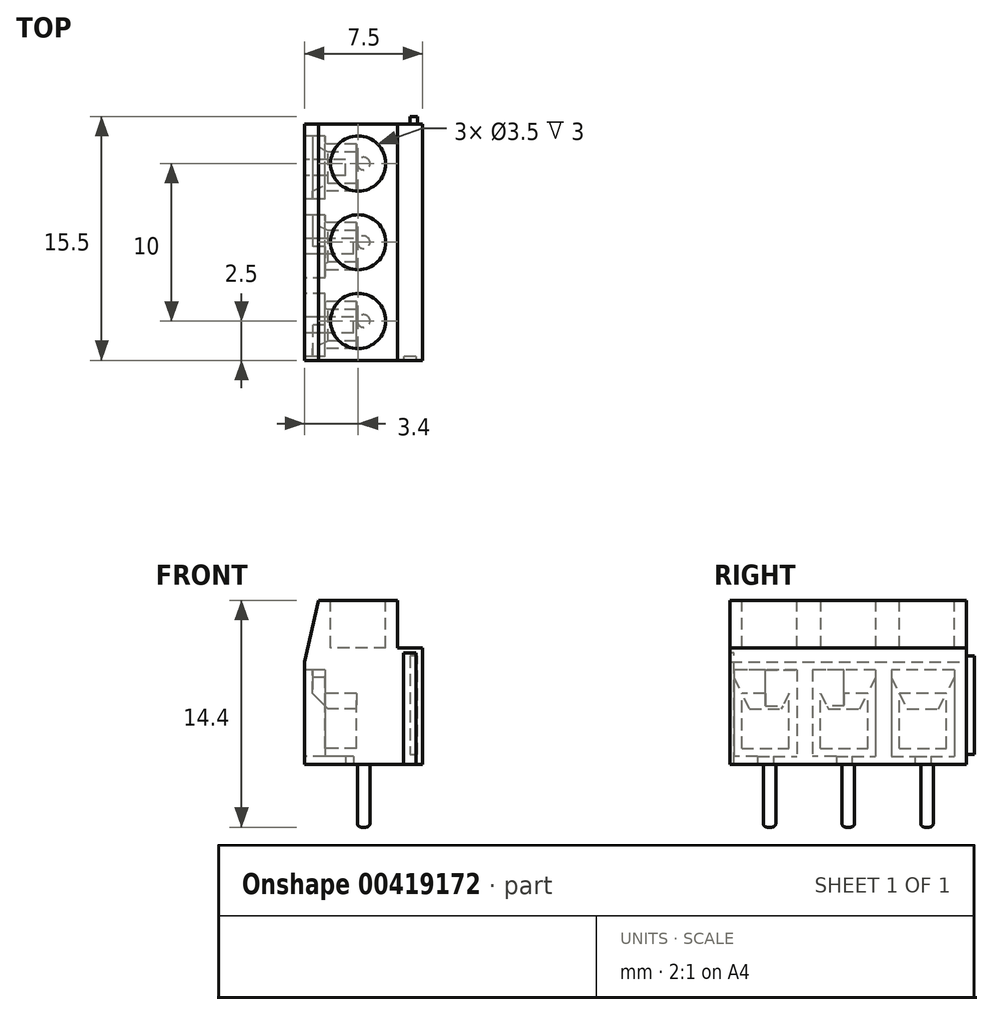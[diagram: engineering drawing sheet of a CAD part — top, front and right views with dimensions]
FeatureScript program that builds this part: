
annotation { "Feature Type Name" : "Feature", "Feature Type Description" : "" }
export const myFeature = defineFeature(function(context is Context, id is Id, definition is map)
    precondition{}
    {
        {
            var Q0;
            Q0=qCreatedBy(makeId("Front.planeOp"),FACE);
            var sketch = newSketch(context, id + "F0", { "sketchPlane" : qUnion([Q0])});
            skLineSegment(sketch, "E0", {"start": v(0, 0) * mm, "end": v(-7.5, 0) * mm});
            skLineSegment(sketch, "E1", {"start": v(-7.5, 0) * mm, "end": v(-7.5, 6.5) * mm});
            skLineSegment(sketch, "E2", {"start": v(-7.5, 6.5) * mm, "end": v(-6.6, 10.4) * mm});
            skLineSegment(sketch, "E3", {"start": v(-6.6, 10.4) * mm, "end": v(-1.6, 10.4) * mm});
            skLineSegment(sketch, "E4", {"start": v(-1.6, 10.4) * mm, "end": v(-1.6, 7.4) * mm});
            skLineSegment(sketch, "E5", {"start": v(-1.6, 7.4) * mm, "end": v(0, 7.4) * mm});
            skLineSegment(sketch, "E6", {"start": v(0, 7.4) * mm, "end": v(0, 0) * mm});
            skSolve(sketch);
        }
        {
            var Q0;
            Q0 = qSketchRegion(id + "F0", true);
            extrude(context, id + "F1", {"entities" : qUnion([Q0]), "depth" : 15 * mm});
        }
        {
            var Q0;
            Q0=makeQuery(id+"F1.opExtrude","SWEPT_FACE",FACE,{"disambiguationData":[OSD([sQuery(id+"F0.wireOp",EDGE,"E3")])]});
            var sketch = newSketch(context, id + "F2", { "sketchPlane" : qUnion([Q0])});
            skLineSegment(sketch, "E7", {"start": v(-4.1, 0) * mm, "end": v(-4.1, -15) * mm});
            skLineSegment(sketch, "E8", {"start": v(-4.1, -15) * mm, "end": v(-4.1, -7.5) * mm});
            skCircle(sketch, "E9", {"center": v(-4.1, -7.5) * mm, "radius": 1.75 * mm});
            skLineSegment(sketch, "E10", {"start": v(-4.1, -7.5) * mm, "end": v(-4.1, -2.5) * mm});
            skCircle(sketch, "E11", {"center": v(-4.1, -2.5) * mm, "radius": 1.75 * mm});
            skLineSegment(sketch, "E12", {"start": v(-4.1, -7.5) * mm, "end": v(4.92, -7.5) * mm});
            skCircle(sketch, "E13.MirrorC", {"center": v(-4.1, -12.5) * mm, "radius": 1.75 * mm});
            skSolve(sketch);
        }
        {
            var Q0;
            Q0 = qSketchRegion(id + "F2", true);
            extrude(context, id + "F3", {"entities" : qUnion([Q0]), "operationType" : NewBodyOperationType.REMOVE, "oppositeDirection" : true, "depth" : 3 * mm});
        }
        {
            var Q0;
            Q0=makeQuery(id+"F1.opExtrude","SWEPT_FACE",FACE,{"disambiguationData":[OSD([sQuery(id+"F0.wireOp",EDGE,"E1")])]});
            var sketch = newSketch(context, id + "F4", { "sketchPlane" : qUnion([Q0])});
            skLineSegment(sketch, "E14", {"start": v(0, 0) * mm, "end": v(15, 0) * mm});
            skLineSegment(sketch, "E15", {"start": v(15, 0) * mm, "end": v(7.76, 0) * mm});
            skLineSegment(sketch, "E16", {"start": v(7.76, 0) * mm, "end": v(7.76, 0.5) * mm});
            skLineSegment(sketch, "E17", {"start": v(7.76, 0.5) * mm, "end": v(7.76, 1) * mm});
            skLineSegment(sketch, "E18", {"start": v(7.76, 1) * mm, "end": v(7.76, 3.5) * mm});
            skLineSegment(sketch, "E19", {"start": v(7.76, 3.5) * mm, "end": v(7.76, 5.5) * mm});
            skLineSegment(sketch, "E20", {"start": v(7.76, 5.5) * mm, "end": v(7.76, 6) * mm});
            skLineSegment(sketch, "E21", {"start": v(7.76, 6) * mm, "end": v(9.76, 6) * mm});
            skLineSegment(sketch, "E22", {"start": v(9.76, 6) * mm, "end": v(9.76, 0.5) * mm});
            skLineSegment(sketch, "E23", {"start": v(7.76, 0.5) * mm, "end": v(9.76, 0.5) * mm});
            skLineSegment(sketch, "E24", {"start": v(9.76, 6) * mm, "end": v(9.76, 5.5) * mm});
            skLineSegment(sketch, "E25", {"start": v(9.76, 5.5) * mm, "end": v(8.76, 3.5) * mm});
            skLineSegment(sketch, "E26", {"start": v(7.76, 3.5) * mm, "end": v(8.76, 3.5) * mm});
            skLineSegment(sketch, "E27", {"start": v(7.76, 1) * mm, "end": v(9.26, 1) * mm});
            skLineSegment(sketch, "E28", {"start": v(9.26, 1) * mm, "end": v(9.26, 4.5) * mm});
            skLineSegment(sketch, "E29", {"start": v(8.26, 0.5) * mm, "end": v(8.26, 0) * mm});
            skLineSegment(sketch, "E30.MirrorCS", {"start": v(5.76, 6) * mm, "end": v(5.76, 5.5) * mm});
            skLineSegment(sketch, "E31.MirrorCS", {"start": v(7.26, 0.5) * mm, "end": v(7.26, 0) * mm});
            skLineSegment(sketch, "E32.MirrorCS", {"start": v(7.76, 1) * mm, "end": v(6.26, 1) * mm});
            skLineSegment(sketch, "E33.MirrorCS", {"start": v(5.76, 6) * mm, "end": v(5.76, 0.5) * mm});
            skLineSegment(sketch, "E34.MirrorCS", {"start": v(7.76, 0.5) * mm, "end": v(5.76, 0.5) * mm});
            skLineSegment(sketch, "E35.MirrorCS", {"start": v(7.76, 6) * mm, "end": v(5.76, 6) * mm});
            skLineSegment(sketch, "E36.MirrorCS", {"start": v(7.76, 3.5) * mm, "end": v(6.76, 3.5) * mm});
            skLineSegment(sketch, "E37.MirrorCS", {"start": v(6.26, 1) * mm, "end": v(6.26, 4.5) * mm});
            skLineSegment(sketch, "E38.MirrorCS", {"start": v(5.76, 5.5) * mm, "end": v(6.76, 3.5) * mm});
            skLineSegment(sketch, "E39.1.0.0", {"start": v(12.76, 1) * mm, "end": v(14.26, 1) * mm});
            skLineSegment(sketch, "E39.1.0.1", {"start": v(14.26, 1) * mm, "end": v(14.26, 4.5) * mm});
            skLineSegment(sketch, "E39.1.0.2", {"start": v(14.76, 5.5) * mm, "end": v(13.76, 3.5) * mm});
            skLineSegment(sketch, "E39.1.0.3", {"start": v(14.76, 6) * mm, "end": v(14.76, 5.5) * mm});
            skLineSegment(sketch, "E39.1.0.4", {"start": v(12.76, 0.5) * mm, "end": v(14.76, 0.5) * mm});
            skLineSegment(sketch, "E39.1.0.5", {"start": v(12.76, 6) * mm, "end": v(14.76, 6) * mm});
            skLineSegment(sketch, "E39.1.0.6", {"start": v(14.76, 6) * mm, "end": v(14.76, 0.5) * mm});
            skLineSegment(sketch, "E39.1.0.7", {"start": v(12.76, 5.5) * mm, "end": v(12.76, 6) * mm});
            skLineSegment(sketch, "E39.1.0.8", {"start": v(10.76, 6) * mm, "end": v(10.76, 0.5) * mm});
            skLineSegment(sketch, "E39.1.0.9", {"start": v(12.76, 1) * mm, "end": v(11.26, 1) * mm});
            skLineSegment(sketch, "E39.1.0.10", {"start": v(10.76, 6) * mm, "end": v(10.76, 5.5) * mm});
            skLineSegment(sketch, "E39.1.0.11", {"start": v(12.76, 3.5) * mm, "end": v(11.76, 3.5) * mm});
            skLineSegment(sketch, "E39.1.0.12", {"start": v(12.76, 6) * mm, "end": v(10.76, 6) * mm});
            skLineSegment(sketch, "E39.1.0.13", {"start": v(12.76, 3.5) * mm, "end": v(13.76, 3.5) * mm});
            skLineSegment(sketch, "E39.1.0.14", {"start": v(10.76, 5.5) * mm, "end": v(11.76, 3.5) * mm});
            skLineSegment(sketch, "E39.1.0.15", {"start": v(12.76, 0.5) * mm, "end": v(10.76, 0.5) * mm});
            skLineSegment(sketch, "E39.1.0.16", {"start": v(12.76, 1) * mm, "end": v(12.76, 3.5) * mm});
            skLineSegment(sketch, "E39.1.0.17", {"start": v(12.76, 3.5) * mm, "end": v(12.76, 5.5) * mm});
            skLineSegment(sketch, "E39.1.0.18", {"start": v(11.26, 1) * mm, "end": v(11.26, 4.5) * mm});
            skLineSegment(sketch, "E39.1.0.19", {"start": v(12.26, 0.5) * mm, "end": v(12.26, 0) * mm});
            skLineSegment(sketch, "E39.1.0.20", {"start": v(13.26, 0.5) * mm, "end": v(13.26, 0) * mm});
            skLineSegment(sketch, "E39.1.0.21", {"start": v(12.76, 1) * mm, "end": v(12.76, 3.5) * mm});
            skLineSegment(sketch, "E39.1.0.22", {"start": v(12.76, 5.5) * mm, "end": v(12.76, 6) * mm});
            skLineSegment(sketch, "E39.1.0.23", {"start": v(12.76, 0) * mm, "end": v(12.76, 0.5) * mm});
            skLineSegment(sketch, "E39.1.0.24", {"start": v(12.76, 0) * mm, "end": v(12.76, 0.5) * mm});
            skLineSegment(sketch, "E39.1.0.25", {"start": v(12.76, 0.5) * mm, "end": v(12.76, 1) * mm});
            skLineSegment(sketch, "E39.1.0.26", {"start": v(12.76, 0.5) * mm, "end": v(12.76, 1) * mm});
            skLineSegment(sketch, "E39.direction1", {"start": v(5.76, 0.5) * mm, "end": v(10.76, 0.5) * mm, "construction": true});
            skLineSegment(sketch, "E40.MirrorCS", {"start": v(2.76, 0.5) * mm, "end": v(2.76, 1) * mm});
            skLineSegment(sketch, "E41.MirrorCS", {"start": v(2.76, 5.5) * mm, "end": v(2.76, 6) * mm});
            skLineSegment(sketch, "E42.MirrorCS", {"start": v(2.76, 0) * mm, "end": v(2.76, 0.5) * mm});
            skLineSegment(sketch, "E43.MirrorCS", {"start": v(4.76, 6) * mm, "end": v(4.76, 5.5) * mm});
            skLineSegment(sketch, "E44.MirrorCS", {"start": v(0.76, 6) * mm, "end": v(0.76, 5.5) * mm});
            skLineSegment(sketch, "E45.MirrorCS", {"start": v(2.76, 3.5) * mm, "end": v(1.76, 3.5) * mm});
            skLineSegment(sketch, "E46.MirrorCS", {"start": v(2.26, 0.5) * mm, "end": v(2.26, 0) * mm});
            skLineSegment(sketch, "E47.MirrorCS", {"start": v(3.26, 0.5) * mm, "end": v(3.26, 0) * mm});
            skLineSegment(sketch, "E48.MirrorCS", {"start": v(2.76, 1) * mm, "end": v(2.76, 3.5) * mm});
            skLineSegment(sketch, "E49.MirrorCS", {"start": v(2.76, 0.5) * mm, "end": v(0.76, 0.5) * mm});
            skLineSegment(sketch, "E50.MirrorCS", {"start": v(2.76, 3.5) * mm, "end": v(2.76, 5.5) * mm});
            skLineSegment(sketch, "E51.MirrorCS", {"start": v(1.26, 1) * mm, "end": v(1.26, 4.5) * mm});
            skLineSegment(sketch, "E52.MirrorCS", {"start": v(4.76, 6) * mm, "end": v(4.76, 0.5) * mm});
            skLineSegment(sketch, "E53.MirrorCS", {"start": v(2.76, 3.5) * mm, "end": v(3.76, 3.5) * mm});
            skLineSegment(sketch, "E54.MirrorCS", {"start": v(2.76, 0.5) * mm, "end": v(4.76, 0.5) * mm});
            skLineSegment(sketch, "E55.MirrorCS", {"start": v(4.76, 5.5) * mm, "end": v(3.76, 3.5) * mm});
            skLineSegment(sketch, "E56.MirrorCS", {"start": v(0.76, 6) * mm, "end": v(0.76, 0.5) * mm});
            skLineSegment(sketch, "E57.MirrorCS", {"start": v(2.76, 6) * mm, "end": v(4.76, 6) * mm});
            skLineSegment(sketch, "E58.MirrorCS", {"start": v(2.76, 1) * mm, "end": v(4.26, 1) * mm});
            skLineSegment(sketch, "E59.MirrorCS", {"start": v(0.76, 5.5) * mm, "end": v(1.76, 3.5) * mm});
            skLineSegment(sketch, "E60.MirrorCS", {"start": v(4.26, 1) * mm, "end": v(4.26, 4.5) * mm});
            skLineSegment(sketch, "E61.MirrorCS", {"start": v(2.76, 1) * mm, "end": v(1.26, 1) * mm});
            skLineSegment(sketch, "E62.MirrorCS", {"start": v(2.76, 6) * mm, "end": v(0.76, 6) * mm});
            skSolve(sketch);
        }
        {
            var Q0;
            Q0 = qSketchRegion(id + "F4", true);
            var Q1;
            {var subQ2=sQuery(id+"F4.wireOp",EDGE,"E45.MirrorCS");Q1=makeQuery(id+"F4.imprint","IMPRINT",FACE,{"disambiguationData":[TD([[makeQuery(id+"F4.imprint","IMPRINT",EDGE,{"derivedFrom":subQ2}),1.0]])]});}
            var Q2;
            {var subQ1=sQuery(id+"F4.wireOp",EDGE,"E53.MirrorCS");Q2=makeQuery(id+"F4.imprint","IMPRINT",FACE,{"disambiguationData":[TD([[makeQuery(id+"F4.imprint","IMPRINT",EDGE,{"derivedFrom":subQ1}),-1.0]])]});}
            var Q3;
            Q3=makeQuery(id+"F4.imprint","IMPRINT",FACE,{"disambiguationData":[TD([[makeQuery(id+"F4.imprint","IMPRINT",EDGE,{"derivedFrom":sQuery(id+"F4.wireOp",EDGE,"E32.MirrorCS")}),-1.0]])]});
            var Q4;
            {var subQ1=sQuery(id+"F4.wireOp",EDGE,"E26");Q4=makeQuery(id+"F4.imprint","IMPRINT",FACE,{"disambiguationData":[TD([[makeQuery(id+"F4.imprint","IMPRINT",EDGE,{"derivedFrom":subQ1}),-1.0]])]});}
            var Q5;
            Q5=makeQuery(id+"F4.imprint","IMPRINT",FACE,{"disambiguationData":[TD([[makeQuery(id+"F4.imprint","IMPRINT",EDGE,{"derivedFrom":sQuery(id+"F4.wireOp",EDGE,"E39.1.0.9")}),-1.0]])]});
            var Q6;
            Q6=makeQuery(id+"F4.imprint","IMPRINT",FACE,{"disambiguationData":[TD([[makeQuery(id+"F4.imprint","IMPRINT",EDGE,{"derivedFrom":sQuery(id+"F4.wireOp",EDGE,"E39.1.0.0")}),1.0]])]});
            extrude(context, id + "F5", {"entities" : qUnion([Q0, Q1, Q2, Q3, Q4, Q5, Q6]), "operationType" : NewBodyOperationType.REMOVE, "oppositeDirection" : true, "depth" : .5 * mm});
        }
        {
            var Q0;
            {var subQ5=sQuery(id+"F4.wireOp",EDGE,"E40.MirrorCS");Q0=makeQuery(id+"F4.imprint","IMPRINT",FACE,{"disambiguationData":[TD([[makeQuery(id+"F4.imprint","IMPRINT",EDGE,{"derivedFrom":subQ5}),1.0]])]});}
            var Q1;
            {var subQ2=sQuery(id+"F4.wireOp",EDGE,"E45.MirrorCS");Q1=makeQuery(id+"F4.imprint","IMPRINT",FACE,{"disambiguationData":[TD([[makeQuery(id+"F4.imprint","IMPRINT",EDGE,{"derivedFrom":subQ2}),1.0]])]});}
            var Q2;
            {var subQ1=sQuery(id+"F4.wireOp",EDGE,"E53.MirrorCS");Q2=makeQuery(id+"F4.imprint","IMPRINT",FACE,{"disambiguationData":[TD([[makeQuery(id+"F4.imprint","IMPRINT",EDGE,{"derivedFrom":subQ1}),-1.0]])]});}
            var Q3;
            {var subQ4=sQuery(id+"F4.wireOp",EDGE,"E40.MirrorCS");Q3=makeQuery(id+"F4.imprint","IMPRINT",FACE,{"disambiguationData":[TD([[makeQuery(id+"F4.imprint","IMPRINT",EDGE,{"derivedFrom":subQ4}),-1.0]])]});}
            var Q4;
            {var subQ1=sQuery(id+"F4.wireOp",EDGE,"E17");Q4=makeQuery(id+"F4.imprint","IMPRINT",FACE,{"disambiguationData":[TD([[makeQuery(id+"F4.imprint","IMPRINT",EDGE,{"derivedFrom":subQ1}),1.0]])]});}
            var Q5;
            Q5=makeQuery(id+"F4.imprint","IMPRINT",FACE,{"disambiguationData":[TD([[makeQuery(id+"F4.imprint","IMPRINT",EDGE,{"derivedFrom":sQuery(id+"F4.wireOp",EDGE,"E32.MirrorCS")}),-1.0]])]});
            var Q6;
            {var subQ1=sQuery(id+"F4.wireOp",EDGE,"E26");Q6=makeQuery(id+"F4.imprint","IMPRINT",FACE,{"disambiguationData":[TD([[makeQuery(id+"F4.imprint","IMPRINT",EDGE,{"derivedFrom":subQ1}),-1.0]])]});}
            var Q7;
            {var subQ1=sQuery(id+"F4.wireOp",EDGE,"E22");Q7=makeQuery(id+"F4.imprint","IMPRINT",FACE,{"disambiguationData":[TD([[makeQuery(id+"F4.imprint","IMPRINT",EDGE,{"derivedFrom":subQ1}),-1.0]])]});}
            var Q8;
            {var subQ4=sQuery(id+"F4.wireOp",EDGE,"E39.1.0.8");Q8=makeQuery(id+"F4.imprint","IMPRINT",FACE,{"disambiguationData":[TD([[makeQuery(id+"F4.imprint","IMPRINT",EDGE,{"derivedFrom":subQ4}),1.0]])]});}
            var Q9;
            Q9=makeQuery(id+"F4.imprint","IMPRINT",FACE,{"disambiguationData":[TD([[makeQuery(id+"F4.imprint","IMPRINT",EDGE,{"derivedFrom":sQuery(id+"F4.wireOp",EDGE,"E39.1.0.9")}),-1.0]])]});
            var Q10;
            Q10=makeQuery(id+"F4.imprint","IMPRINT",FACE,{"disambiguationData":[TD([[makeQuery(id+"F4.imprint","IMPRINT",EDGE,{"derivedFrom":sQuery(id+"F4.wireOp",EDGE,"E39.1.0.0")}),1.0]])]});
            var Q11;
            Q11=makeQuery(id+"F4.imprint","IMPRINT",FACE,{"disambiguationData":[TD([[makeQuery(id+"F4.imprint","IMPRINT",EDGE,{"derivedFrom":sQuery(id+"F4.wireOp",EDGE,"E39.1.0.0")}),-1.0]])]});
            extrude(context, id + "F6", {"entities" : qUnion([Q0, Q1, Q2, Q3, Q4, Q5, Q6, Q7, Q8, Q9, Q10, Q11]), "operationType" : NewBodyOperationType.REMOVE, "oppositeDirection" : true, "depth" : 1.3 * mm});
        }
        {
            var Q0;
            {var subQ2=sQuery(id+"F4.wireOp",EDGE,"E45.MirrorCS");Q0=makeQuery(id+"F4.imprint","IMPRINT",FACE,{"disambiguationData":[TD([[makeQuery(id+"F4.imprint","IMPRINT",EDGE,{"derivedFrom":subQ2}),1.0]])]});}
            var Q1;
            {var subQ1=sQuery(id+"F4.wireOp",EDGE,"E53.MirrorCS");Q1=makeQuery(id+"F4.imprint","IMPRINT",FACE,{"disambiguationData":[TD([[makeQuery(id+"F4.imprint","IMPRINT",EDGE,{"derivedFrom":subQ1}),-1.0]])]});}
            var Q2;
            Q2=makeQuery(id+"F4.imprint","IMPRINT",FACE,{"disambiguationData":[TD([[makeQuery(id+"F4.imprint","IMPRINT",EDGE,{"derivedFrom":sQuery(id+"F4.wireOp",EDGE,"E32.MirrorCS")}),-1.0]])]});
            var Q3;
            {var subQ1=sQuery(id+"F4.wireOp",EDGE,"E26");Q3=makeQuery(id+"F4.imprint","IMPRINT",FACE,{"disambiguationData":[TD([[makeQuery(id+"F4.imprint","IMPRINT",EDGE,{"derivedFrom":subQ1}),-1.0]])]});}
            var Q4;
            Q4=makeQuery(id+"F4.imprint","IMPRINT",FACE,{"disambiguationData":[TD([[makeQuery(id+"F4.imprint","IMPRINT",EDGE,{"derivedFrom":sQuery(id+"F4.wireOp",EDGE,"E39.1.0.9")}),-1.0]])]});
            var Q5;
            Q5=makeQuery(id+"F4.imprint","IMPRINT",FACE,{"disambiguationData":[TD([[makeQuery(id+"F4.imprint","IMPRINT",EDGE,{"derivedFrom":sQuery(id+"F4.wireOp",EDGE,"E39.1.0.0")}),1.0]])]});
            extrude(context, id + "F7", {"entities" : qUnion([Q0, Q1, Q2, Q3, Q4, Q5]), "operationType" : NewBodyOperationType.REMOVE, "oppositeDirection" : true, "depth" : 3.3 * mm});
        }
        {
            var Q0;
            Q0=makeQuery(id+"F6.boolean.opBoolean","INTERSECT",EDGE,{"derivedFrom":[makeQuery(id+"F5.boolean.opBoolean","COPY",FACE,{"derivedFrom":makeQuery(id+"F5.opExtrude","CAP_FACE",FACE,{"disambiguationData":[OSD([sQuery(id+"F4.wireOp",EDGE,"E14"),sQuery(id+"F4.wireOp",EDGE,"E46.MirrorCS"),sQuery(id+"F4.wireOp",EDGE,"E47.MirrorCS"),sQuery(id+"F4.wireOp",EDGE,"E49.MirrorCS"),sQuery(id+"F4.wireOp",EDGE,"E52.MirrorCS"),sQuery(id+"F4.wireOp",EDGE,"E54.MirrorCS"),sQuery(id+"F4.wireOp",EDGE,"E56.MirrorCS"),sQuery(id+"F4.wireOp",EDGE,"E57.MirrorCS"),sQuery(id+"F4.wireOp",EDGE,"E62.MirrorCS")])],"isStart":false})}),makeQuery(id+"F6.opExtrude","SWEPT_FACE",FACE,{"disambiguationData":[OSD([sQuery(id+"F4.wireOp",EDGE,"E45.MirrorCS"),sQuery(id+"F4.wireOp",EDGE,"E53.MirrorCS")])]})]});
            var Q1;
            Q1=makeQuery(id+"F6.boolean.opBoolean","INTERSECT",EDGE,{"derivedFrom":[makeQuery(id+"F5.boolean.opBoolean","COPY",FACE,{"derivedFrom":makeQuery(id+"F5.opExtrude","CAP_FACE",FACE,{"disambiguationData":[OSD([sQuery(id+"F4.wireOp",EDGE,"E14"),sQuery(id+"F4.wireOp",EDGE,"E15"),sQuery(id+"F4.wireOp",EDGE,"E21"),sQuery(id+"F4.wireOp",EDGE,"E22"),sQuery(id+"F4.wireOp",EDGE,"E23"),sQuery(id+"F4.wireOp",EDGE,"E24"),sQuery(id+"F4.wireOp",EDGE,"E29"),sQuery(id+"F4.wireOp",EDGE,"E31.MirrorCS"),sQuery(id+"F4.wireOp",EDGE,"E33.MirrorCS"),sQuery(id+"F4.wireOp",EDGE,"E34.MirrorCS"),sQuery(id+"F4.wireOp",EDGE,"E35.MirrorCS")])],"isStart":false})}),makeQuery(id+"F6.opExtrude","SWEPT_FACE",FACE,{"disambiguationData":[OSD([sQuery(id+"F4.wireOp",EDGE,"E26"),sQuery(id+"F4.wireOp",EDGE,"E36.MirrorCS")])]})]});
            var Q2;
            Q2=makeQuery(id+"F6.boolean.opBoolean","INTERSECT",EDGE,{"derivedFrom":[makeQuery(id+"F5.boolean.opBoolean","COPY",FACE,{"derivedFrom":makeQuery(id+"F5.opExtrude","CAP_FACE",FACE,{"disambiguationData":[OSD([sQuery(id+"F4.wireOp",EDGE,"E15"),sQuery(id+"F4.wireOp",EDGE,"E39.1.0.4"),sQuery(id+"F4.wireOp",EDGE,"E39.1.0.5"),sQuery(id+"F4.wireOp",EDGE,"E39.1.0.6"),sQuery(id+"F4.wireOp",EDGE,"E39.1.0.8"),sQuery(id+"F4.wireOp",EDGE,"E39.1.0.10"),sQuery(id+"F4.wireOp",EDGE,"E39.1.0.12"),sQuery(id+"F4.wireOp",EDGE,"E39.1.0.15"),sQuery(id+"F4.wireOp",EDGE,"E39.1.0.19"),sQuery(id+"F4.wireOp",EDGE,"E39.1.0.20")])],"isStart":false})}),makeQuery(id+"F6.opExtrude","SWEPT_FACE",FACE,{"disambiguationData":[OSD([sQuery(id+"F4.wireOp",EDGE,"E39.1.0.11"),sQuery(id+"F4.wireOp",EDGE,"E39.1.0.13")])]})]});
            chamfer(context, id + "F8", {"entities" : qUnion([Q0, Q1, Q2]), "width" : 1 * mm, "tangentPropagation" : true});
        }
        {
            var Q0;
            Q0=makeQuery(id+"F1.opExtrude","CAP_FACE",FACE,{"disambiguationData":[OSD([sQuery(id+"F0.wireOp",EDGE,"E0"),sQuery(id+"F0.wireOp",EDGE,"E1"),sQuery(id+"F0.wireOp",EDGE,"E2"),sQuery(id+"F0.wireOp",EDGE,"E3"),sQuery(id+"F0.wireOp",EDGE,"E4"),sQuery(id+"F0.wireOp",EDGE,"E5"),sQuery(id+"F0.wireOp",EDGE,"E6")])],"isStart":false});
            var sketch = newSketch(context, id + "F9", { "sketchPlane" : qUnion([Q0])});
            skLineSegment(sketch, "E63", {"start": v(0, 0) * mm, "end": v(-0.42, 0) * mm});
            skLineSegment(sketch, "E64", {"start": v(-0.42, 0) * mm, "end": v(-0.42, 7.05) * mm});
            skLineSegment(sketch, "E65", {"start": v(-0.42, 7.05) * mm, "end": v(-1.21, 7.05) * mm});
            skLineSegment(sketch, "E66", {"start": v(-1.21, 7.05) * mm, "end": v(-1.21, 0) * mm});
            skLineSegment(sketch, "E67", {"start": v(-1.21, 0) * mm, "end": v(-0.42, 0) * mm});
            skSolve(sketch);
        }
        {
            var Q0;
            Q0 = qSketchRegion(id + "F9", true);
            extrude(context, id + "F10", {"entities" : qUnion([Q0]), "operationType" : NewBodyOperationType.REMOVE, "oppositeDirection" : true, "depth" : .25 * mm});
        }
        {
            var Q0;
            Q0=makeQuery(id+"F1.opExtrude","CAP_FACE",FACE,{"disambiguationData":[OSD([sQuery(id+"F0.wireOp",EDGE,"E0"),sQuery(id+"F0.wireOp",EDGE,"E1"),sQuery(id+"F0.wireOp",EDGE,"E2"),sQuery(id+"F0.wireOp",EDGE,"E3"),sQuery(id+"F0.wireOp",EDGE,"E4"),sQuery(id+"F0.wireOp",EDGE,"E5"),sQuery(id+"F0.wireOp",EDGE,"E6")])],"isStart":true});
            var sketch = newSketch(context, id + "F11", { "sketchPlane" : qUnion([Q0])});
            skLineSegment(sketch, "E68", {"start": v(0, 0) * mm, "end": v(0.31, 0) * mm});
            skLineSegment(sketch, "E69", {"start": v(0.31, 0) * mm, "end": v(0.31, 6.87) * mm});
            skLineSegment(sketch, "E70", {"start": v(0.31, 6.87) * mm, "end": v(0.81, 6.87) * mm});
            skLineSegment(sketch, "E71", {"start": v(0.81, 6.87) * mm, "end": v(0.81, 0.61) * mm});
            skLineSegment(sketch, "E72", {"start": v(0.81, 0.61) * mm, "end": v(0.31, 0.61) * mm});
            skSolve(sketch);
        }
        {
            var Q0;
            Q0 = qSketchRegion(id + "F11", true);
            extrude(context, id + "F12", {"entities" : qUnion([Q0]), "operationType" : NewBodyOperationType.ADD, "depth" : .5 * mm});
        }
        {
            var Q0;
            Q0=makeQuery(id+"F1.opExtrude","SWEPT_FACE",FACE,{"disambiguationData":[OSD([sQuery(id+"F0.wireOp",EDGE,"E0")])]});
            var sketch = newSketch(context, id + "F13", { "sketchPlane" : qUnion([Q0])});
            skLineSegment(sketch, "E73", {"start": v(-7.5, 15) * mm, "end": v(0, 15) * mm});
            skLineSegment(sketch, "E74", {"start": v(0, 15) * mm, "end": v(-3.75, 15) * mm});
            skLineSegment(sketch, "E75", {"start": v(-3.75, 15) * mm, "end": v(-3.75, 0) * mm});
            skLineSegment(sketch, "E76", {"start": v(-3.75, 0) * mm, "end": v(-3.75, 7.5) * mm});
            skLineSegment(sketch, "E77", {"start": v(-3.75, 7.5) * mm, "end": v(-3.75, 12.5) * mm});
            skCircle(sketch, "E78", {"center": v(-3.75, 7.5) * mm, "radius": 0.4 * mm});
            skCircle(sketch, "E79", {"center": v(-3.75, 12.5) * mm, "radius": 0.4 * mm});
            skLineSegment(sketch, "E80", {"start": v(-3.75, 7.5) * mm, "end": v(-3.35, 7.5) * mm});
            skCircle(sketch, "E81.MirrorC", {"center": v(-3.75, 2.5) * mm, "radius": 0.4 * mm});
            skSolve(sketch);
        }
        {
            var Q0;
            Q0 = qSketchRegion(id + "F13", true);
            extrude(context, id + "F14", {"entities" : qUnion([Q0]), "operationType" : NewBodyOperationType.ADD, "depth" : 4 * mm});
        }
        {
            var Q0;
            Q0=makeQuery(id+"F14.opExtrude","CAP_EDGE",EDGE,{"disambiguationData":[OSD([sQuery(id+"F13.wireOp",EDGE,"E79")])],"isStart":false});
            var Q1;
            Q1=makeQuery(id+"F14.opExtrude","CAP_EDGE",EDGE,{"disambiguationData":[OSD([sQuery(id+"F13.wireOp",EDGE,"E78")])],"isStart":false});
            var Q2;
            Q2=makeQuery(id+"F14.opExtrude","CAP_EDGE",EDGE,{"disambiguationData":[OSD([sQuery(id+"F13.wireOp",EDGE,"E81.MirrorC")])],"isStart":false});
            fillet(context, id + "F15", {"entities" : qUnion([Q0, Q1, Q2]), "radius" : .25 * mm, "tangentPropagation" : true, "allowEdgeOverflow" : false});
        }
        {
            var Q0;
            {var subQ0=sQuery(id+"F4.wireOp",EDGE,"E39.1.0.15");var subQ1=sQuery(id+"F4.wireOp",EDGE,"E39.1.0.19");var subQ2=sQuery(id+"F4.wireOp",EDGE,"E39.1.0.4");var subQ3=sQuery(id+"F4.wireOp",EDGE,"E39.1.0.20");Q0=makeQuery(id+"F6.boolean.opBoolean","SPLIT",FACE,{"disambiguationData":[TD([makeQuery(id+"F1.opExtrude","SWEPT_FACE",FACE,{"disambiguationData":[OSD([sQuery(id+"F0.wireOp",EDGE,"E0")])]})])],"derivedFrom":makeQuery(id+"F5.boolean.opBoolean","COPY",FACE,{"derivedFrom":makeQuery(id+"F5.opExtrude","CAP_FACE",FACE,{"disambiguationData":[OSD([sQuery(id+"F4.wireOp",EDGE,"E15"),subQ2,sQuery(id+"F4.wireOp",EDGE,"E39.1.0.5"),sQuery(id+"F4.wireOp",EDGE,"E39.1.0.6"),sQuery(id+"F4.wireOp",EDGE,"E39.1.0.8"),sQuery(id+"F4.wireOp",EDGE,"E39.1.0.10"),sQuery(id+"F4.wireOp",EDGE,"E39.1.0.12"),subQ0,subQ1,subQ3])],"isStart":false})})});}
            var Q1;
            {var subQ0=sQuery(id+"F4.wireOp",EDGE,"E29");var subQ1=sQuery(id+"F4.wireOp",EDGE,"E23");var subQ2=sQuery(id+"F4.wireOp",EDGE,"E31.MirrorCS");var subQ3=sQuery(id+"F4.wireOp",EDGE,"E34.MirrorCS");Q1=makeQuery(id+"F6.boolean.opBoolean","SPLIT",FACE,{"disambiguationData":[TD([makeQuery(id+"F1.opExtrude","SWEPT_FACE",FACE,{"disambiguationData":[OSD([sQuery(id+"F0.wireOp",EDGE,"E0")])]})])],"derivedFrom":makeQuery(id+"F5.boolean.opBoolean","COPY",FACE,{"derivedFrom":makeQuery(id+"F5.opExtrude","CAP_FACE",FACE,{"disambiguationData":[OSD([sQuery(id+"F4.wireOp",EDGE,"E14"),sQuery(id+"F4.wireOp",EDGE,"E15"),sQuery(id+"F4.wireOp",EDGE,"E21"),sQuery(id+"F4.wireOp",EDGE,"E22"),subQ1,sQuery(id+"F4.wireOp",EDGE,"E24"),subQ0,subQ2,sQuery(id+"F4.wireOp",EDGE,"E33.MirrorCS"),subQ3,sQuery(id+"F4.wireOp",EDGE,"E35.MirrorCS")])],"isStart":false})})});}
            var Q2;
            {var subQ0=sQuery(id+"F4.wireOp",EDGE,"E42.MirrorCS");Q2=makeQuery(id+"F4.imprint","IMPRINT",FACE,{"disambiguationData":[TD([[makeQuery(id+"F4.imprint","IMPRINT",EDGE,{"derivedFrom":subQ0}),-1.0]])]});}
            var Q3;
            {var subQ0=sQuery(id+"F4.wireOp",EDGE,"E42.MirrorCS");Q3=makeQuery(id+"F4.imprint","IMPRINT",FACE,{"disambiguationData":[TD([[makeQuery(id+"F4.imprint","IMPRINT",EDGE,{"derivedFrom":subQ0}),1.0]])]});}
            extrude(context, id + "F16", {"entities" : qUnion([Q0, Q1, Q2, Q3]), "operationType" : NewBodyOperationType.REMOVE, "oppositeDirection" : true, "depth" : 2.6 * mm});
        }
    });
